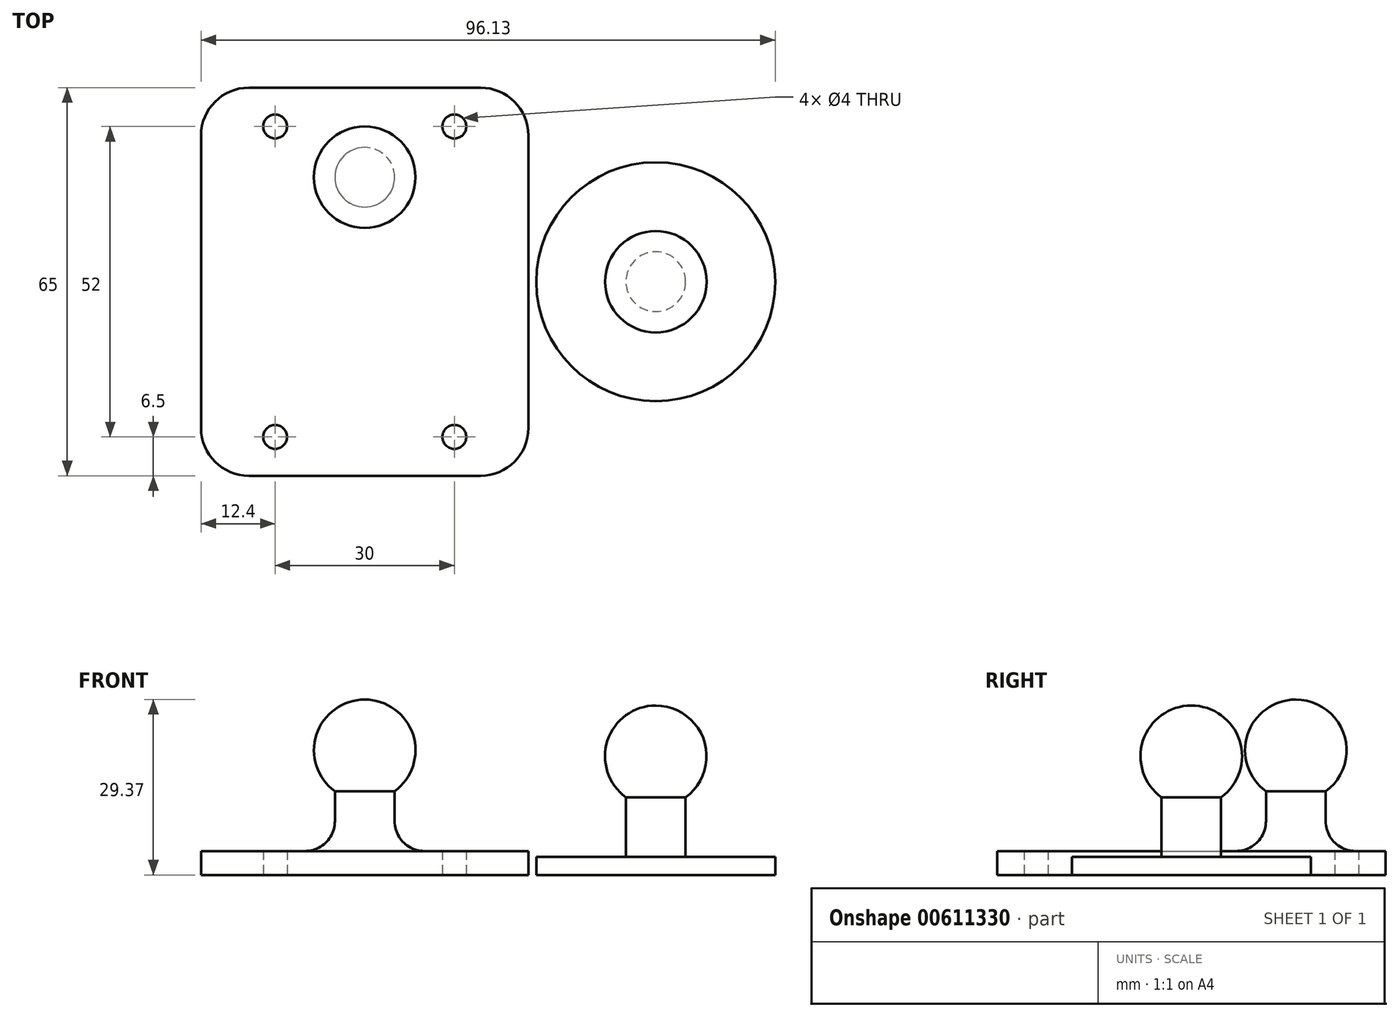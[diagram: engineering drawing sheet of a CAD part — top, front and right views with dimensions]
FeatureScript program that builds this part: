
annotation { "Feature Type Name" : "Feature", "Feature Type Description" : "" }
export const myFeature = defineFeature(function(context is Context, id is Id, definition is map)
    precondition{}
    {
        {
            var Q0;
            Q0=qCreatedBy(makeId("Top.planeOp"),FACE);
            var sketch = newSketch(context, id + "F0", { "sketchPlane" : qUnion([Q0])});
            skLineSegment(sketch, "E0.bottom", {"start": v(-19.4, -32.5) * mm, "end": v(19.4, -32.5) * mm});
            skLineSegment(sketch, "E0.top", {"start": v(-19.4, 32.5) * mm, "end": v(19.4, 32.5) * mm});
            skLineSegment(sketch, "E0.left", {"start": v(-27.4, -24.5) * mm, "end": v(-27.4, 24.5) * mm});
            skLineSegment(sketch, "E0.right", {"start": v(27.4, -24.5) * mm, "end": v(27.4, 24.5) * mm});
            skPoint(sketch, "E0.middle", {"position": v(0, 0) * mm});
            skPoint(sketch, "E1.visualSharp", {"position": v(-27.4, 32.5) * mm});
            skArc(sketch, "E1.filletArc", {"start": v(-19.4, 32.5) * mm, "mid": v(-25.06, 30.16) * mm, "end": v(-27.4, 24.5) * mm});
            skPoint(sketch, "E2.visualSharp", {"position": v(27.4, 32.5) * mm});
            skArc(sketch, "E2.filletArc", {"start": v(27.4, 24.5) * mm, "mid": v(25.06, 30.16) * mm, "end": v(19.4, 32.5) * mm});
            skPoint(sketch, "E3.visualSharp", {"position": v(27.4, -32.5) * mm});
            skArc(sketch, "E3.filletArc", {"start": v(19.4, -32.5) * mm, "mid": v(25.06, -30.16) * mm, "end": v(27.4, -24.5) * mm});
            skPoint(sketch, "E4.visualSharp", {"position": v(-27.4, -32.5) * mm});
            skArc(sketch, "E4.filletArc", {"start": v(-27.4, -24.5) * mm, "mid": v(-25.06, -30.16) * mm, "end": v(-19.4, -32.5) * mm});
            skCircle(sketch, "E5", {"center": v(-15, 26) * mm, "radius": 2 * mm});
            skCircle(sketch, "E6", {"center": v(15, 26) * mm, "radius": 2 * mm});
            skCircle(sketch, "E7", {"center": v(15, -26) * mm, "radius": 2 * mm});
            skCircle(sketch, "E8", {"center": v(-15, -26) * mm, "radius": 2 * mm});
            skSolve(sketch);
        }
        {
            var Q0;
            Q0=makeQuery(id+"F0.imprint","IMPRINT",FACE,{"disambiguationData":[TD([[makeQuery(id+"F0.imprint","IMPRINT",EDGE,{"derivedFrom":sQuery(id+"F0.wireOp",EDGE,"E0.bottom")}),1.0]])]});
            extrude(context, id + "F1", {"entities" : qUnion([Q0]), "depth" : 4 * mm, "offsetDistance" : 25 * mm});
        }
        {
            var Q0;
            Q0=qCreatedBy(makeId("Right.planeOp"),FACE);
            var sketch = newSketch(context, id + "F2", { "sketchPlane" : qUnion([Q0])});
            skLineSegment(sketch, "E9", {"start": v(17.5, 0) * mm, "end": v(22.5, 0) * mm});
            skLineSegment(sketch, "E10", {"start": v(22.5, 0) * mm, "end": v(22.5, 14) * mm});
            skArc(sketch, "E11", {"start": v(22.5, 14) * mm, "mid": v(25.58, 23.5) * mm, "end": v(17.5, 29.37) * mm});
            skLineSegment(sketch, "E12", {"start": v(17.5, 20.87) * mm, "end": v(17.5, 29.37) * mm});
            skLineSegment(sketch, "E13", {"start": v(17.5, 20.87) * mm, "end": v(17.5, 0) * mm});
            skSolve(sketch);
        }
        {
            var Q0;
            Q0 = qSketchRegion(id + "F2", true);
            var Q1;
            Q1=sQuery(id+"F2.wireOp",EDGE,"E13");
            revolve(context, id + "F3", {"operationType" : NewBodyOperationType.ADD, "entities" : qUnion([Q0]), "axis" : qUnion([Q1]), "revolveType" : RevolveType.FULL});
        }
        {
            var Q0;
            Q0=makeQuery(id+"F3.boolean.opBoolean","INTERSECT",EDGE,{"derivedFrom":[makeQuery(id+"F1.opExtrude","CAP_FACE",FACE,{"disambiguationData":[OSD([sQuery(id+"F0.wireOp",EDGE,"E0.bottom"),sQuery(id+"F0.wireOp",EDGE,"E0.top"),sQuery(id+"F0.wireOp",EDGE,"E0.left"),sQuery(id+"F0.wireOp",EDGE,"E0.right"),sQuery(id+"F0.wireOp",EDGE,"E1.filletArc"),sQuery(id+"F0.wireOp",EDGE,"E2.filletArc"),sQuery(id+"F0.wireOp",EDGE,"E3.filletArc"),sQuery(id+"F0.wireOp",EDGE,"E4.filletArc"),sQuery(id+"F0.wireOp",EDGE,"E5"),sQuery(id+"F0.wireOp",EDGE,"E6"),sQuery(id+"F0.wireOp",EDGE,"E7"),sQuery(id+"F0.wireOp",EDGE,"E8")])],"isStart":false}),makeQuery(id+"F3.opRevolve","SWEPT_FACE",FACE,{"disambiguationData":[OSD([sQuery(id+"F2.wireOp",EDGE,"E10")])]})]});
            fillet(context, id + "F4", {"entities" : qUnion([Q0]), "radius" : 5 * mm, "tangentPropagation" : true, "allowEdgeOverflow" : false});
        }
        {
            var Q0;
            Q0=qCreatedBy(makeId("Front.planeOp"),FACE);
            var sketch = newSketch(context, id + "F5", { "sketchPlane" : qUnion([Q0])});
            skLineSegment(sketch, "E14", {"start": v(48.73, 19.87) * mm, "end": v(48.73, -9.73) * mm});
            skLineSegment(sketch, "E15", {"start": v(48.73, 0) * mm, "end": v(68.73, 0) * mm});
            skLineSegment(sketch, "E16", {"start": v(68.73, 0) * mm, "end": v(68.73, 3) * mm});
            skLineSegment(sketch, "E17", {"start": v(68.73, 3) * mm, "end": v(53.73, 3) * mm});
            skLineSegment(sketch, "E18", {"start": v(53.73, 3) * mm, "end": v(53.73, 13) * mm});
            skArc(sketch, "E19", {"start": v(53.73, 13) * mm, "mid": v(56.81, 22.5) * mm, "end": v(48.73, 28.37) * mm});
            skLineSegment(sketch, "E20", {"start": v(48.73, 19.87) * mm, "end": v(48.73, 50.03) * mm});
            skSolve(sketch);
        }
        {
            var Q0;
            {var subQ0=sQuery(id+"F5.wireOp",EDGE,"E15");Q0=makeQuery(id+"F5.imprint","IMPRINT",FACE,{"disambiguationData":[TD([[makeQuery(id+"F5.imprint","IMPRINT",EDGE,{"derivedFrom":subQ0}),1.0]])]});}
            var Q1;
            Q1=sQuery(id+"F5.wireOp",EDGE,"E14");
            revolve(context, id + "F6", {"entities" : qUnion([Q0]), "axis" : qUnion([Q1]), "revolveType" : RevolveType.FULL});
        }
    });
